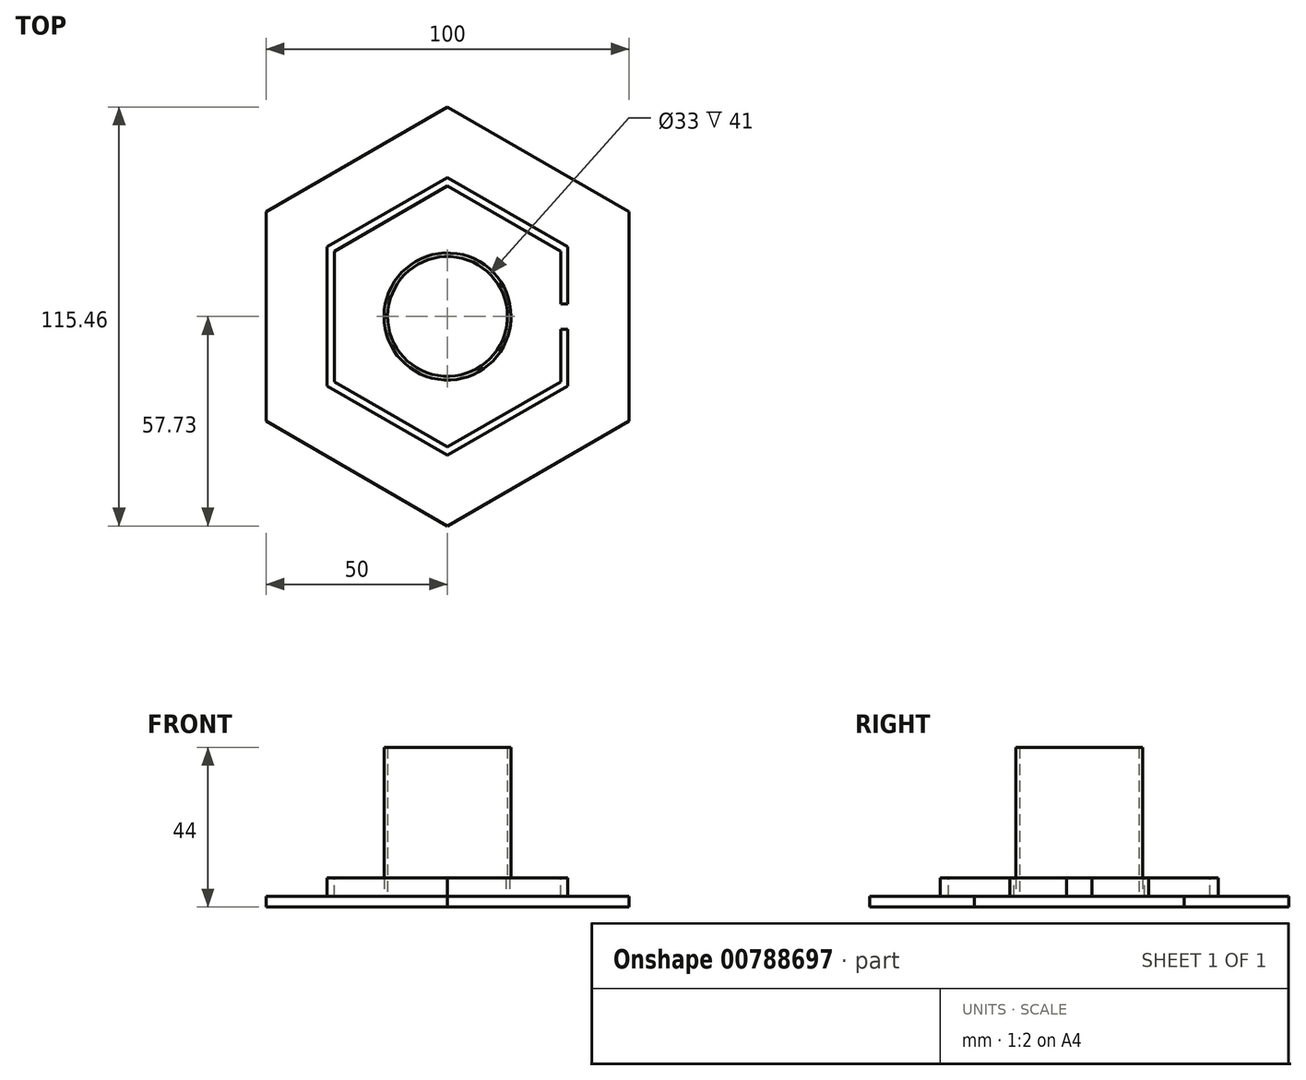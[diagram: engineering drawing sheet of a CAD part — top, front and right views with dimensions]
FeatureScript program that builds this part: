
annotation { "Feature Type Name" : "Feature", "Feature Type Description" : "" }
export const myFeature = defineFeature(function(context is Context, id is Id, definition is map)
    precondition{}
    {
        {
            var Q0;
            Q0=qCreatedBy(makeId("Top.planeOp"),FACE);
            var sketch = newSketch(context, id + "F0", { "sketchPlane" : qUnion([Q0])});
            skCircle(sketch, "E0.cCircle", {"center": v(0, 0) * mm, "radius": 50 * mm, "construction": true});
            skLineSegment(sketch, "E0.0", {"start": v(0, 57.73) * mm, "end": v(50, 28.87) * mm});
            skLineSegment(sketch, "E0.1", {"start": v(50, 28.87) * mm, "end": v(50, -28.87) * mm});
            skLineSegment(sketch, "E0.2", {"start": v(50, -28.87) * mm, "end": v(0, -57.73) * mm});
            skLineSegment(sketch, "E0.3", {"start": v(0, -57.73) * mm, "end": v(-50, -28.87) * mm});
            skLineSegment(sketch, "E0.4", {"start": v(-50, -28.87) * mm, "end": v(-50, 28.87) * mm});
            skLineSegment(sketch, "E0.5", {"start": v(-50, 28.87) * mm, "end": v(0, 57.73) * mm});
            skPoint(sketch, "E0.0.midPoint", {"position": v(25, 43.3) * mm});
            skSolve(sketch);
        }
        {
            var Q0;
            Q0=qSketchRegion(id+"F0",true);
            extrude(context, id + "F1", {"entities" : qUnion([Q0]), "depth" : 3 * mm, "offsetDistance" : 25 * mm});
        }
        {
            var Q0;
            Q0=makeQuery(id+"F1.opExtrude","CAP_FACE",FACE,{"disambiguationData":[OSD([sQuery(id+"F0.wireOp",EDGE,"E0.0"),sQuery(id+"F0.wireOp",EDGE,"E0.1"),sQuery(id+"F0.wireOp",EDGE,"E0.2"),sQuery(id+"F0.wireOp",EDGE,"E0.3"),sQuery(id+"F0.wireOp",EDGE,"E0.4"),sQuery(id+"F0.wireOp",EDGE,"E0.5")])],"isStart":false});
            var sketch = newSketch(context, id + "F2", { "sketchPlane" : qUnion([Q0])});
            skCircle(sketch, "E1.cCircle", {"center": v(0, 0) * mm, "radius": 33.14 * mm, "construction": true});
            skLineSegment(sketch, "E1.0", {"start": v(0, 38.27) * mm, "end": v(33.14, 19.14) * mm});
            skLineSegment(sketch, "E1.1", {"start": v(33.14, 19.14) * mm, "end": v(33.14, -19.14) * mm});
            skLineSegment(sketch, "E1.2", {"start": v(33.14, -19.14) * mm, "end": v(0, -38.27) * mm});
            skLineSegment(sketch, "E1.3", {"start": v(0, -38.27) * mm, "end": v(-33.14, -19.14) * mm});
            skLineSegment(sketch, "E1.4", {"start": v(-33.14, -19.14) * mm, "end": v(-33.14, 19.14) * mm});
            skLineSegment(sketch, "E1.5", {"start": v(-33.14, 19.14) * mm, "end": v(0, 38.27) * mm});
            skPoint(sketch, "E1.0.midPoint", {"position": v(16.57, 28.7) * mm});
            skSolve(sketch);
        }
        {
            var Q0;
            Q0=qSketchRegion(id+"F2",true);
            extrude(context, id + "F3", {"entities" : qUnion([Q0]), "operationType" : NewBodyOperationType.ADD, "depth" : 5 * mm, "offsetDistance" : 25 * mm});
        }
        {
            var Q0;
            Q0=makeQuery(id+"F3.opExtrude","CAP_FACE",FACE,{"disambiguationData":[OSD([sQuery(id+"F2.wireOp",EDGE,"E1.0"),sQuery(id+"F2.wireOp",EDGE,"E1.1"),sQuery(id+"F2.wireOp",EDGE,"E1.2"),sQuery(id+"F2.wireOp",EDGE,"E1.3"),sQuery(id+"F2.wireOp",EDGE,"E1.4"),sQuery(id+"F2.wireOp",EDGE,"E1.5")])],"isStart":false});
            var sketch = newSketch(context, id + "F4", { "sketchPlane" : qUnion([Q0])});
            skCircle(sketch, "E2.cCircle", {"center": v(0, 0) * mm, "radius": 31.14 * mm, "construction": true});
            skLineSegment(sketch, "E2.0", {"start": v(0, 35.96) * mm, "end": v(31.14, 17.98) * mm});
            skLineSegment(sketch, "E2.1", {"start": v(31.14, 17.98) * mm, "end": v(31.14, -17.98) * mm});
            skLineSegment(sketch, "E2.2", {"start": v(31.14, -17.98) * mm, "end": v(0, -35.96) * mm});
            skLineSegment(sketch, "E2.3", {"start": v(0, -35.96) * mm, "end": v(-31.14, -17.98) * mm});
            skLineSegment(sketch, "E2.4", {"start": v(-31.14, -17.98) * mm, "end": v(-31.14, 17.98) * mm});
            skLineSegment(sketch, "E2.5", {"start": v(-31.14, 17.98) * mm, "end": v(0, 35.96) * mm});
            skPoint(sketch, "E2.0.midPoint", {"position": v(15.57, 26.97) * mm});
            skSolve(sketch);
        }
        {
            var Q0;
            Q0=qSketchRegion(id+"F4",true);
            extrude(context, id + "F5", {"entities" : qUnion([Q0]), "operationType" : NewBodyOperationType.REMOVE, "oppositeDirection" : true, "depth" : 5 * mm, "offsetDistance" : 25 * mm});
        }
        {
            var Q0;
            Q0=makeQuery(id+"F5.boolean.opBoolean","COPY",FACE,{"derivedFrom":makeQuery(id+"F5.opExtrude","CAP_FACE",FACE,{"disambiguationData":[OSD([sQuery(id+"F4.wireOp",EDGE,"E2.0"),sQuery(id+"F4.wireOp",EDGE,"E2.1"),sQuery(id+"F4.wireOp",EDGE,"E2.2"),sQuery(id+"F4.wireOp",EDGE,"E2.3"),sQuery(id+"F4.wireOp",EDGE,"E2.4"),sQuery(id+"F4.wireOp",EDGE,"E2.5")])],"isStart":false})});
            var sketch = newSketch(context, id + "F6", { "sketchPlane" : qUnion([Q0])});
            skCircle(sketch, "E3", {"center": v(0, 0) * mm, "radius": 17.5 * mm});
            skCircle(sketch, "E4", {"center": v(0, 0) * mm, "radius": 16.5 * mm});
            skSolve(sketch);
        }
        {
            var Q0;
            Q0=makeQuery(id+"F6.imprint","IMPRINT",FACE,{"disambiguationData":[TD([[makeQuery(id+"F6.imprint","IMPRINT",EDGE,{"derivedFrom":sQuery(id+"F6.wireOp",EDGE,"E3")}),1.0]])]});
            var Q1;
            Q1=sQuery(id+"F6.wireOp",EDGE,"E4");
            var Q2;
            Q2=sQuery(id+"F6.wireOp",EDGE,"E3");
            extrude(context, id + "F7", {"entities" : qUnion([Q0]), "operationType" : NewBodyOperationType.ADD, "surfaceOperationType" : NewSurfaceOperationType.ADD, "surfaceEntities" : qUnion([Q1, Q2]), "depth" : 41 * mm, "offsetDistance" : 25 * mm});
        }
        {
            var Q0;
            Q0=makeQuery(id+"F3.opExtrude","SWEPT_FACE",FACE,{"disambiguationData":[OSD([sQuery(id+"F2.wireOp",EDGE,"E1.1")])]});
            var sketch = newSketch(context, id + "F8", { "sketchPlane" : qUnion([Q0])});
            skPoint(sketch, "E5", {"position": v(0, 5.5) * mm});
            skPoint(sketch, "E5.positionSnap0", {"position": v(0, 8) * mm});
            skPoint(sketch, "E5.positionSnap1", {"position": v(-19.14, 5.5) * mm});
            skLineSegment(sketch, "E6.bottom", {"start": v(0, 3) * mm, "end": v(-3.5, 3) * mm});
            skLineSegment(sketch, "E6.top", {"start": v(0, 7) * mm, "end": v(-3.5, 7) * mm});
            skLineSegment(sketch, "E6.left", {"start": v(0, 3) * mm, "end": v(0, 7) * mm});
            skLineSegment(sketch, "E6.right", {"start": v(-3.5, 3) * mm, "end": v(-3.5, 7) * mm});
            skLineSegment(sketch, "E7.bottom", {"start": v(0, 7) * mm, "end": v(3.5, 7) * mm});
            skLineSegment(sketch, "E7.top", {"start": v(0, 3) * mm, "end": v(3.5, 3) * mm});
            skLineSegment(sketch, "E7.left", {"start": v(0, 7) * mm, "end": v(0, 3) * mm});
            skLineSegment(sketch, "E7.right", {"start": v(3.5, 7) * mm, "end": v(3.5, 3) * mm});
            skLineSegment(sketch, "E8.bottom", {"start": v(-3.5, 7) * mm, "end": v(3.5, 7) * mm});
            skLineSegment(sketch, "E8.top", {"start": v(-3.5, 8) * mm, "end": v(3.5, 8) * mm});
            skLineSegment(sketch, "E8.left", {"start": v(-3.5, 7) * mm, "end": v(-3.5, 8) * mm});
            skLineSegment(sketch, "E8.right", {"start": v(3.5, 7) * mm, "end": v(3.5, 8) * mm});
            skSolve(sketch);
        }
        {
            var Q0;
            Q0 = qSketchRegion(id + "F8", true);
            extrude(context, id + "F9", {"entities" : qUnion([Q0]), "operationType" : NewBodyOperationType.REMOVE, "oppositeDirection" : true, "depth" : 25 * mm, "offsetDistance" : 25 * mm});
        }
    });
